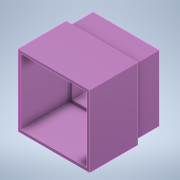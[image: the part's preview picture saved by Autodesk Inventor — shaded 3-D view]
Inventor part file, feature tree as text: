
AUTODESK INVENTOR PART (.ipt)
format: ipt  version: 2022.1 (Build 261234000, 234)  size: 151,552 bytes
history: native  units: mm
features: extrude x4, sketch x3
ambient origin geometry x8: Origin, YZ Plane, XZ Plane, XY Plane, X Axis, Y Axis, Z Axis, Center Point
bodies: Body1 (feature_tree)
feature tree (7):
  sketch  "Sketch18"  dims[d102=46.5mm d103=46.5mm]
  extrude  "Extrusion14"  Depth=46.5mm
  extrude  "Extrusion15"  Depth=2.5mm
  extrude  "Extrusion16"  Depth=2.0mm TaperAngle=0.0deg
  extrude  "Extrusion17"  Depth=15.0mm TaperAngle=0.0deg
  sketch  "Sketch19"  dims[d104=2.5mm d105=2.5mm]
  sketch  "Sketch21"  dims[d106=5.2mm d107=2.0mm d108=0.0mm d109=15.0mm d110=0.0mm d111=2.0mm d112=2.0mm d113=34.0mm d114=0.0mm d119=25.4mm d120=0.0mm d121=0.0mm]
